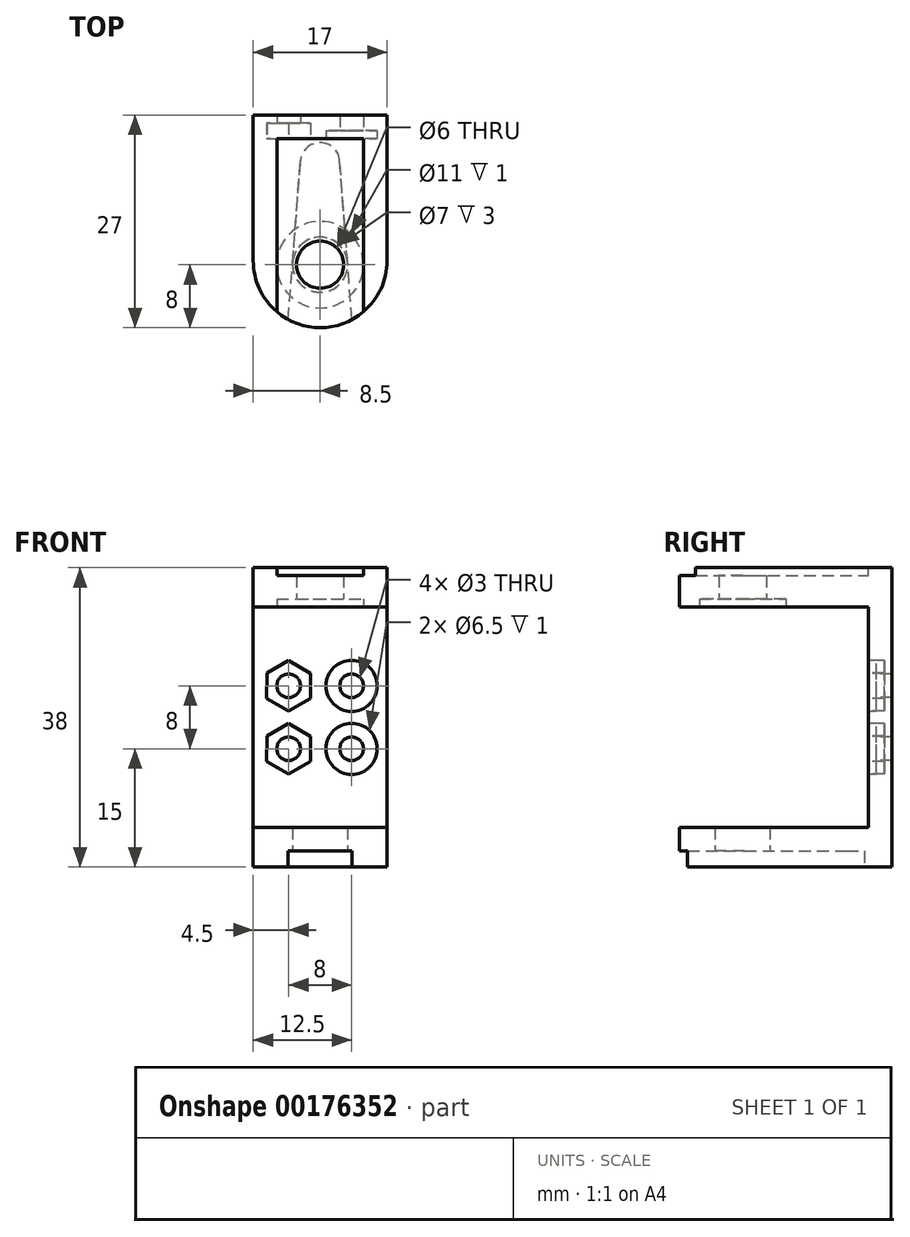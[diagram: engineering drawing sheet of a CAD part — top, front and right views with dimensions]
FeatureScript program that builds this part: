
annotation { "Feature Type Name" : "Feature", "Feature Type Description" : "" }
export const myFeature = defineFeature(function(context is Context, id is Id, definition is map)
    precondition{}
    {
        {
            var Q0;
            Q0=qCreatedBy(makeId("Front.planeOp"),FACE);
            var sketch = newSketch(context, id + "F0", { "sketchPlane" : qUnion([Q0])});
            skLineSegment(sketch, "E0.bottom", {"start": v(8.5, 19) * mm, "end": v(-8.5, 19) * mm});
            skLineSegment(sketch, "E0.top", {"start": v(8.5, -19) * mm, "end": v(-8.5, -19) * mm});
            skLineSegment(sketch, "E0.left", {"start": v(8.5, 19) * mm, "end": v(8.5, -19) * mm});
            skLineSegment(sketch, "E0.right", {"start": v(-8.5, 19) * mm, "end": v(-8.5, -19) * mm});
            skPoint(sketch, "E0.middle", {"position": v(0, 0) * mm});
            skSolve(sketch);
        }
        {
            var Q0;
            Q0 = qSketchRegion(id + "F0", true);
            extrude(context, id + "F1", {"entities" : qUnion([Q0]), "depth" : 3 * mm});
        }
        {
            var Q0;
            Q0=makeQuery(id+"F1.opExtrude","CAP_FACE",FACE,{"disambiguationData":[OSD([sQuery(id+"F0.wireOp",EDGE,"E0.bottom"),sQuery(id+"F0.wireOp",EDGE,"E0.top"),sQuery(id+"F0.wireOp",EDGE,"E0.left"),sQuery(id+"F0.wireOp",EDGE,"E0.right")])],"isStart":false});
            var sketch = newSketch(context, id + "F2", { "sketchPlane" : qUnion([Q0])});
            skLineSegment(sketch, "E1.bottom", {"start": v(-8.5, -19) * mm, "end": v(8.5, -19) * mm});
            skLineSegment(sketch, "E1.top", {"start": v(-8.5, -14) * mm, "end": v(8.5, -14) * mm});
            skLineSegment(sketch, "E1.left", {"start": v(-8.5, -19) * mm, "end": v(-8.5, -14) * mm});
            skLineSegment(sketch, "E1.right", {"start": v(8.5, -19) * mm, "end": v(8.5, -14) * mm});
            skLineSegment(sketch, "E2.MirrorCS", {"start": v(-8.5, 14) * mm, "end": v(8.5, 14) * mm});
            skLineSegment(sketch, "E3.MirrorCS", {"start": v(-8.5, 19) * mm, "end": v(-8.5, 14) * mm});
            skLineSegment(sketch, "E4.MirrorCS", {"start": v(-8.5, 19) * mm, "end": v(8.5, 19) * mm});
            skLineSegment(sketch, "E5.MirrorCS", {"start": v(8.5, 19) * mm, "end": v(8.5, 14) * mm});
            skSolve(sketch);
        }
        {
            var Q0;
            Q0 = qSketchRegion(id + "F2", true);
            extrude(context, id + "F3", {"entities" : qUnion([Q0]), "operationType" : NewBodyOperationType.ADD, "depth" : 24 * mm});
        }
        {
            var Q0;
            Q0=makeQuery(id+"F3.opExtrude","CAP_EDGE",EDGE,{"disambiguationData":[OSD([sQuery(id+"F2.wireOp",EDGE,"E1.right")])],"isStart":false});
            var Q1;
            Q1=makeQuery(id+"F3.opExtrude","CAP_EDGE",EDGE,{"disambiguationData":[OSD([sQuery(id+"F2.wireOp",EDGE,"E1.left")])],"isStart":false});
            var Q2;
            Q2=makeQuery(id+"F3.opExtrude","CAP_EDGE",EDGE,{"disambiguationData":[OSD([sQuery(id+"F2.wireOp",EDGE,"E5.MirrorCS")])],"isStart":false});
            var Q3;
            Q3=makeQuery(id+"F3.opExtrude","CAP_EDGE",EDGE,{"disambiguationData":[OSD([sQuery(id+"F2.wireOp",EDGE,"E3.MirrorCS")])],"isStart":false});
            fillet(context, id + "F4", {"entities" : qUnion([Q0, Q1, Q2, Q3]), "radius" : 8.5 * mm, "tangentPropagation" : true, "allowEdgeOverflow" : false});
        }
        {
            var Q0;
            Q0=makeQuery(id+"F3.boolean.opBoolean","MERGE",FACE,{"derivedFrom":[makeQuery(id+"F1.opExtrude","SWEPT_FACE",FACE,{"disambiguationData":[OSD([sQuery(id+"F0.wireOp",EDGE,"E0.top")])]}),makeQuery(id+"F3.opExtrude","SWEPT_FACE",FACE,{"disambiguationData":[OSD([sQuery(id+"F2.wireOp",EDGE,"E1.bottom")])]})]});
            var sketch = newSketch(context, id + "F5", { "sketchPlane" : qUnion([Q0])});
            skCircle(sketch, "E6", {"center": v(0, 19) * mm, "radius": 3 * mm});
            skSolve(sketch);
        }
        {
            var Q0;
            Q0=makeQuery(id+"F5.imprint","IMPRINT",FACE,{"disambiguationData":[TD([[makeQuery(id+"F5.imprint","IMPRINT",EDGE,{"derivedFrom":sQuery(id+"F5.wireOp",EDGE,"E6")}),1.0]])]});
            extrude(context, id + "F6", {"entities" : qUnion([Q0]), "operationType" : NewBodyOperationType.REMOVE, "oppositeDirection" : true, "depth" : 40 * mm});
        }
        {
            var Q0;
            Q0=makeQuery(id+"F3.boolean.opBoolean","MERGE",FACE,{"derivedFrom":[makeQuery(id+"F1.opExtrude","SWEPT_FACE",FACE,{"disambiguationData":[OSD([sQuery(id+"F0.wireOp",EDGE,"E0.bottom")])]}),makeQuery(id+"F3.opExtrude","SWEPT_FACE",FACE,{"disambiguationData":[OSD([sQuery(id+"F2.wireOp",EDGE,"E4.MirrorCS")])]})]});
            var sketch = newSketch(context, id + "F7", { "sketchPlane" : qUnion([Q0])});
            skLineSegment(sketch, "E7.bottom", {"start": v(5.5, -32.98) * mm, "end": v(-5.5, -32.98) * mm});
            skLineSegment(sketch, "E7.top", {"start": v(5.5, -3) * mm, "end": v(-5.5, -3) * mm});
            skLineSegment(sketch, "E7.left", {"start": v(5.5, -32.98) * mm, "end": v(5.5, -3) * mm});
            skLineSegment(sketch, "E7.right", {"start": v(-5.5, -32.98) * mm, "end": v(-5.5, -3) * mm});
            skSolve(sketch);
        }
        {
            var Q0;
            Q0 = qSketchRegion(id + "F7", true);
            extrude(context, id + "F8", {"entities" : qUnion([Q0]), "operationType" : NewBodyOperationType.REMOVE, "oppositeDirection" : true, "depth" : 1 * mm});
        }
        {
            var Q0;
            Q0=makeQuery(id+"F3.boolean.opBoolean","MERGE",FACE,{"derivedFrom":[makeQuery(id+"F1.opExtrude","SWEPT_FACE",FACE,{"disambiguationData":[OSD([sQuery(id+"F0.wireOp",EDGE,"E0.top")])]}),makeQuery(id+"F3.opExtrude","SWEPT_FACE",FACE,{"disambiguationData":[OSD([sQuery(id+"F2.wireOp",EDGE,"E1.bottom")])]})]});
            var sketch = newSketch(context, id + "F9", { "sketchPlane" : qUnion([Q0])});
            skLineSegment(sketch, "E8", {"start": v(-4.23, 28.38) * mm, "end": v(-2.5, 5.8) * mm});
            skLineSegment(sketch, "E9.MirrorCS", {"start": v(4.23, 28.38) * mm, "end": v(2.5, 5.8) * mm});
            skArc(sketch, "E10", {"start": v(-2.5, 5.8) * mm, "mid": v(0, 3.5) * mm, "end": v(2.5, 5.8) * mm});
            skLineSegment(sketch, "E11", {"start": v(-4.23, 28.38) * mm, "end": v(4.23, 28.38) * mm});
            skCircle(sketch, "E12", {"center": v(0, 19) * mm, "radius": 3.5 * mm});
            skSolve(sketch);
        }
        {
            var Q0;
            Q0 = qSketchRegion(id + "F9", true);
            extrude(context, id + "F10", {"entities" : qUnion([Q0]), "operationType" : NewBodyOperationType.REMOVE, "oppositeDirection" : true, "depth" : 2 * mm});
        }
        {
            var Q0;
            Q0=makeQuery(id+"F3.opExtrude","SWEPT_FACE",FACE,{"disambiguationData":[OSD([sQuery(id+"F2.wireOp",EDGE,"E2.MirrorCS")])]});
            var sketch = newSketch(context, id + "F11", { "sketchPlane" : qUnion([Q0])});
            skCircle(sketch, "E13", {"center": v(0, 19) * mm, "radius": 5.5 * mm});
            skSolve(sketch);
        }
        {
            var Q0;
            Q0 = qSketchRegion(id + "F11", true);
            extrude(context, id + "F12", {"entities" : qUnion([Q0]), "operationType" : NewBodyOperationType.REMOVE, "oppositeDirection" : true, "depth" : 1 * mm});
        }
        {
            var Q0;
            Q0=makeQuery(id+"F1.opExtrude","CAP_FACE",FACE,{"disambiguationData":[OSD([sQuery(id+"F0.wireOp",EDGE,"E0.bottom"),sQuery(id+"F0.wireOp",EDGE,"E0.top"),sQuery(id+"F0.wireOp",EDGE,"E0.left"),sQuery(id+"F0.wireOp",EDGE,"E0.right")])],"isStart":true});
            var sketch = newSketch(context, id + "F13", { "sketchPlane" : qUnion([Q0])});
            skPoint(sketch, "E14", {"position": v(-4, -4) * mm});
            skPoint(sketch, "E15.MirrorP", {"position": v(-4, 4) * mm});
            skSolve(sketch);
        }
        {
            var Q0;
            Q0=sQuery(id+"F13.wireOp",VERTEX,"E15.MirrorP");
            var Q1;
            Q1=sQuery(id+"F13.wireOp",VERTEX,"5d9b686c-818d-4e17-add7-60bd97503a200.MirrorP");
            var Q2;
            Q2=sQuery(id+"F13.wireOp",VERTEX,"E14");
            var Q3;
            Q3=sQuery(id+"F13.wireOp",VERTEX,"a18d2e19-8ac6-4625-9ebd-ed48deb488a20.MirrorP");
            var Q4;
            Q4=makeQuery(id+"F1.opExtrude","SWEPT_BODY",BODY,{"disambiguationData":[OSD([sQuery(id+"F0.wireOp",EDGE,"E0.bottom"),sQuery(id+"F0.wireOp",EDGE,"E0.top"),sQuery(id+"F0.wireOp",EDGE,"E0.left"),sQuery(id+"F0.wireOp",EDGE,"E0.right")])]});
            hole(context, id + "F14", {"style" : HoleStyle.SIMPLE, "endStyle" : HoleEndStyle.BLIND, "holeDiameter" : 1 * mm, "holeDepth" : 20 * mm, "startFromSketch" : true, "locations" : qUnion([Q0, Q1, Q2, Q3]), "scope" : qUnion([Q4])});
        }
        {
            var Q0;
            Q0=makeQuery(id+"F1.opExtrude","CAP_FACE",FACE,{"disambiguationData":[OSD([sQuery(id+"F0.wireOp",EDGE,"E0.bottom"),sQuery(id+"F0.wireOp",EDGE,"E0.top"),sQuery(id+"F0.wireOp",EDGE,"E0.left"),sQuery(id+"F0.wireOp",EDGE,"E0.right")])],"isStart":false});
            var sketch = newSketch(context, id + "F15", { "sketchPlane" : qUnion([Q0])});
            skPoint(sketch, "E16", {"position": v(4, 4) * mm});
            skPoint(sketch, "E17", {"position": v(4, -4) * mm});
            skPoint(sketch, "E18", {"position": v(-4, -4) * mm});
            skSolve(sketch);
        }
        {
            var Q0;
            Q0=sQuery(id+"F15.wireOp",VERTEX,"1e0347c8-6699-4331-95e7-cd0aa3de58a7");
            var Q1;
            Q1=sQuery(id+"F15.wireOp",VERTEX,"E16");
            var Q2;
            Q2=sQuery(id+"F15.wireOp",VERTEX,"E17");
            var Q3;
            Q3=makeQuery(id+"F1.opExtrude","SWEPT_BODY",BODY,{"disambiguationData":[OSD([sQuery(id+"F0.wireOp",EDGE,"E0.bottom"),sQuery(id+"F0.wireOp",EDGE,"E0.top"),sQuery(id+"F0.wireOp",EDGE,"E0.left"),sQuery(id+"F0.wireOp",EDGE,"E0.right")])]});
            hole(context, id + "F16", {"style" : HoleStyle.C_BORE, "endStyle" : HoleEndStyle.BLIND, "holeDiameter" : 3 * mm, "cBoreDiameter" : 6.5 * mm, "cBoreDepth" : 1 * mm, "holeDepth" : 20 * mm, "startFromSketch" : true, "locations" : qUnion([Q0, Q1, Q2]), "scope" : qUnion([Q3])});
        }
        {
            var Q0;
            Q0=makeQuery(id+"F1.opExtrude","CAP_FACE",FACE,{"disambiguationData":[OSD([sQuery(id+"F0.wireOp",EDGE,"E0.bottom"),sQuery(id+"F0.wireOp",EDGE,"E0.top"),sQuery(id+"F0.wireOp",EDGE,"E0.left"),sQuery(id+"F0.wireOp",EDGE,"E0.right")])],"isStart":false});
            var sketch = newSketch(context, id + "F17", { "sketchPlane" : qUnion([Q0])});
            skSolve(sketch);
        }
        {
            var Q0;
            Q0=makeQuery(id+"F10.boolean.opBoolean","COPY",FACE,{"derivedFrom":makeQuery(id+"F10.opExtrude","CAP_FACE",FACE,{"disambiguationData":[OSD([sQuery(id+"F9.wireOp",EDGE,"E8"),sQuery(id+"F9.wireOp",EDGE,"E9.MirrorCS"),sQuery(id+"F9.wireOp",EDGE,"E10"),sQuery(id+"F9.wireOp",EDGE,"E11"),sQuery(id+"F9.wireOp",EDGE,"E12")])],"isStart":false})});
            var sketch = newSketch(context, id + "F18", { "sketchPlane" : qUnion([Q0])});
            skCircle(sketch, "E19", {"center": v(0, 19) * mm, "radius": 3.5 * mm});
            skSolve(sketch);
        }
        {
            var Q0;
            Q0 = qSketchRegion(id + "F18", true);
            extrude(context, id + "F19", {"entities" : qUnion([Q0]), "operationType" : NewBodyOperationType.REMOVE, "oppositeDirection" : true, "depth" : 25 * mm});
        }
        {
            var Q0;
            Q0=makeQuery(id+"F17.imprint","IMPRINT",FACE,{"disambiguationData":[TD([[makeQuery(id+"F17.imprint","IMPRINT",EDGE,{"derivedFrom":makeQuery(id+"F1.opExtrude","CAP_EDGE",EDGE,{"disambiguationData":[OSD([sQuery(id+"F0.wireOp",EDGE,"E0.left")])],"isStart":false})}),-1.0]])]});
            var sketch = newSketch(context, id + "F20", { "sketchPlane" : qUnion([Q0])});
            skPoint(sketch, "E20", {"position": v(4, 4) * mm});
            skPoint(sketch, "E21", {"position": v(-4, 4) * mm});
            skPoint(sketch, "E22", {"position": v(4, -4) * mm});
            skPoint(sketch, "E23", {"position": v(-4, -4) * mm});
            skCircle(sketch, "E24.cCircle", {"center": v(-4, 4) * mm, "radius": 2.77 * mm, "construction": true});
            skLineSegment(sketch, "E24.0", {"start": v(-3.99, 7.2) * mm, "end": v(-1.22, 5.6) * mm});
            skLineSegment(sketch, "E24.1", {"start": v(-1.22, 5.6) * mm, "end": v(-1.23, 2.39) * mm});
            skLineSegment(sketch, "E24.2", {"start": v(-1.23, 2.39) * mm, "end": v(-4.01, 0.8) * mm});
            skLineSegment(sketch, "E24.3", {"start": v(-4.01, 0.8) * mm, "end": v(-6.78, 2.4) * mm});
            skLineSegment(sketch, "E24.4", {"start": v(-6.78, 2.4) * mm, "end": v(-6.77, 5.61) * mm});
            skLineSegment(sketch, "E24.5", {"start": v(-6.77, 5.61) * mm, "end": v(-3.99, 7.2) * mm});
            skPoint(sketch, "E24.0.midPoint", {"position": v(-2.6, 6.4) * mm});
            skCircle(sketch, "E25.cCircle", {"center": v(-4, -4) * mm, "radius": 2.78 * mm, "construction": true});
            skLineSegment(sketch, "E25.0", {"start": v(-3.99, -0.8) * mm, "end": v(-1.22, -2.4) * mm});
            skLineSegment(sketch, "E25.1", {"start": v(-1.22, -2.4) * mm, "end": v(-1.23, -5.61) * mm});
            skLineSegment(sketch, "E25.2", {"start": v(-1.23, -5.61) * mm, "end": v(-4.01, -7.2) * mm});
            skLineSegment(sketch, "E25.3", {"start": v(-4.01, -7.2) * mm, "end": v(-6.78, -5.6) * mm});
            skLineSegment(sketch, "E25.4", {"start": v(-6.78, -5.6) * mm, "end": v(-6.77, -2.39) * mm});
            skLineSegment(sketch, "E25.5", {"start": v(-6.77, -2.39) * mm, "end": v(-3.99, -0.8) * mm});
            skPoint(sketch, "E25.0.midPoint", {"position": v(-2.6, -1.6) * mm});
            skSolve(sketch);
        }
        {
            var Q0;
            Q0 = qSketchRegion(id + "F20", true);
            extrude(context, id + "F21", {"entities" : qUnion([Q0]), "operationType" : NewBodyOperationType.REMOVE, "oppositeDirection" : true, "depth" : 2 * mm});
        }
        {
            var Q0;
            Q0=sQuery(id+"F20.wireOp",VERTEX,"E21");
            var Q1;
            Q1=sQuery(id+"F20.wireOp",VERTEX,"E23");
            var Q2;
            Q2=makeQuery(id+"F1.opExtrude","SWEPT_BODY",BODY,{"disambiguationData":[OSD([sQuery(id+"F0.wireOp",EDGE,"E0.bottom"),sQuery(id+"F0.wireOp",EDGE,"E0.top"),sQuery(id+"F0.wireOp",EDGE,"E0.left"),sQuery(id+"F0.wireOp",EDGE,"E0.right")])]});
            hole(context, id + "F22", {"style" : HoleStyle.SIMPLE, "endStyle" : HoleEndStyle.THROUGH, "holeDiameter" : 3 * mm, "startFromSketch" : true, "locations" : qUnion([Q0, Q1]), "scope" : qUnion([Q2]), "isTappedThrough" : true});
        }
    });
